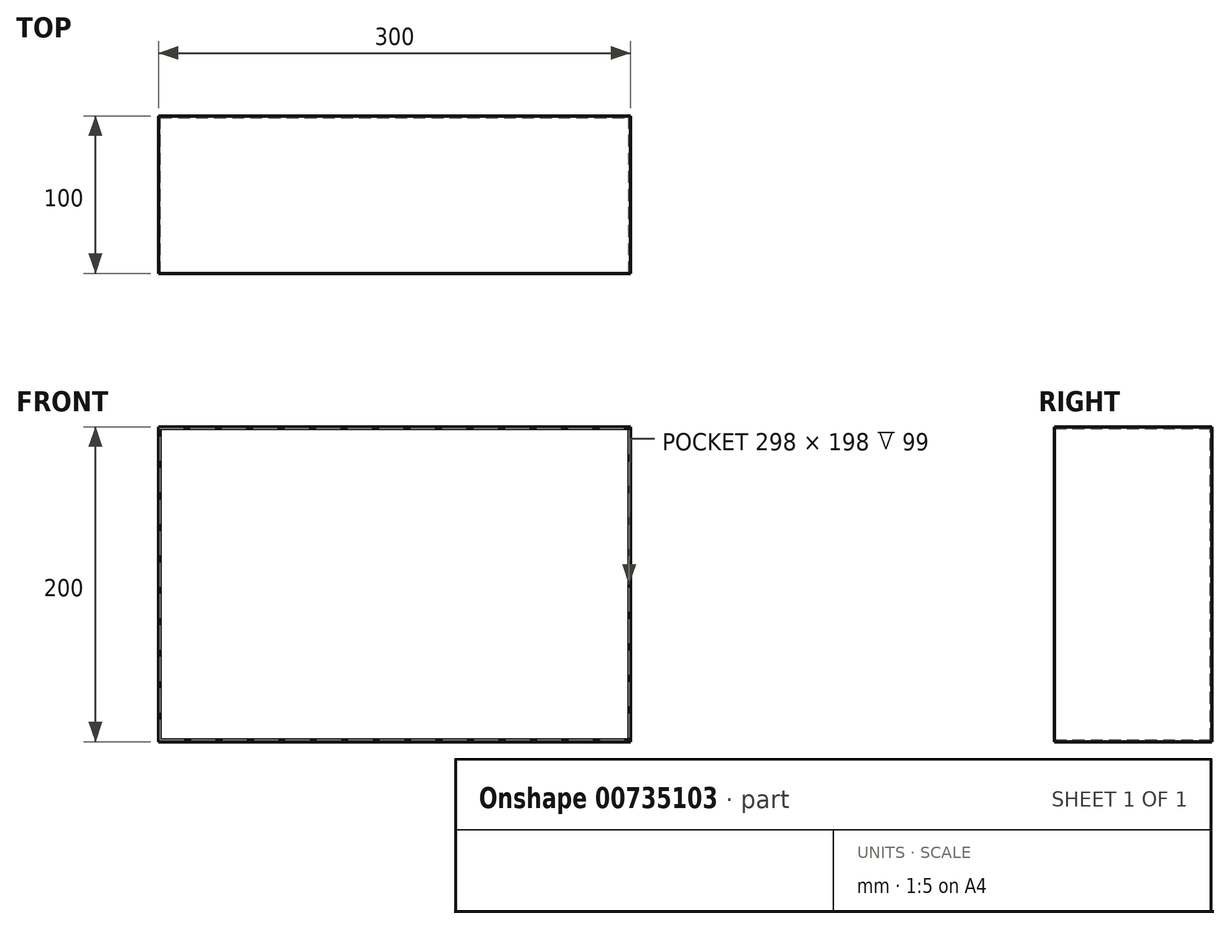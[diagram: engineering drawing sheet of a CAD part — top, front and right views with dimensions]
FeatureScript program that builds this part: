
annotation { "Feature Type Name" : "Feature", "Feature Type Description" : "" }
export const myFeature = defineFeature(function(context is Context, id is Id, definition is map)
    precondition{}
    {
        {
            var Q0;
            Q0=qCreatedBy(makeId("Front.planeOp"),FACE);
            var sketch = newSketch(context, id + "F0", { "sketchPlane" : qUnion([Q0])});
            skLineSegment(sketch, "E0.bottom", {"start": v(150, 100) * mm, "end": v(-150, 100) * mm});
            skLineSegment(sketch, "E0.top", {"start": v(150, -100) * mm, "end": v(-150, -100) * mm});
            skLineSegment(sketch, "E0.left", {"start": v(150, 100) * mm, "end": v(150, -100) * mm});
            skLineSegment(sketch, "E0.right", {"start": v(-150, 100) * mm, "end": v(-150, -100) * mm});
            skPoint(sketch, "E0.middle", {"position": v(0, 0) * mm});
            skLineSegment(sketch, "E1.bottom", {"start": v(149, 99) * mm, "end": v(-149, 99) * mm});
            skLineSegment(sketch, "E1.top", {"start": v(149, -99) * mm, "end": v(-149, -99) * mm});
            skLineSegment(sketch, "E1.left", {"start": v(149, 99) * mm, "end": v(149, -99) * mm});
            skLineSegment(sketch, "E1.right", {"start": v(-149, 99) * mm, "end": v(-149, -99) * mm});
            skSolve(sketch);
        }
        {
            var Q0;
            Q0=makeQuery(id+"F0.imprint","IMPRINT",FACE,{"disambiguationData":[TD([[makeQuery(id+"F0.imprint","IMPRINT",EDGE,{"derivedFrom":sQuery(id+"F0.wireOp",EDGE,"E1.bottom")}),1.0]])]});
            var Q1;
            Q1=makeQuery(id+"F0.imprint","IMPRINT",FACE,{"disambiguationData":[TD([[makeQuery(id+"F0.imprint","IMPRINT",EDGE,{"derivedFrom":sQuery(id+"F0.wireOp",EDGE,"E0.bottom")}),1.0]])]});
            extrude(context, id + "F1", {"entities" : qUnion([Q0, Q1]), "depth" : 1 * mm, "offsetDistance" : 25 * mm});
        }
        {
            var Q0;
            Q0=makeQuery(id+"F0.imprint","IMPRINT",FACE,{"disambiguationData":[TD([[makeQuery(id+"F0.imprint","IMPRINT",EDGE,{"derivedFrom":sQuery(id+"F0.wireOp",EDGE,"E0.bottom")}),1.0]])]});
            extrude(context, id + "F2", {"entities" : qUnion([Q0]), "operationType" : NewBodyOperationType.ADD, "depth" : 100 * mm, "offsetDistance" : 25 * mm});
        }
    });
